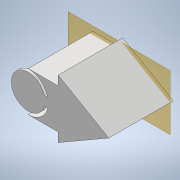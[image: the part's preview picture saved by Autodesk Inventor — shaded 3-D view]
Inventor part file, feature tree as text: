
AUTODESK INVENTOR PART (.ipt)
format: ipt  version: 2022.3 (Build 263350000, 350)  size: 201,216 bytes
history: native  units: mm
features: plane x5, reference x5, sketch x4, extrude x4, other x3
ambient origin geometry x8: Origin, YZ Plane, XZ Plane, XY Plane, X Axis, Y Axis, Z Axis, Center Point
bodies: Solid1 (feature_tree)
feature tree (21):
  sketch  "Sketch1"  dims[d0=10.0mm d1=0.0mm d2=0.2mm]
  other  "Work Point1"
  extrude  "Extrusion1"  Depth=10.0mm
  plane  "Work Plane1"
  sketch  "Sketch2"  dims[d3=1.0mm d4=10.0mm d5=0.0mm]
  plane  "Work Plane2"
  extrude  "Extrusion2"  Depth=10.0mm TaperAngle=0.0deg
  plane  "Work Plane3"
  sketch  "Sketch3"  dims[d6=10.0mm d7=0.0mm d8=2.0mm d9=0.0mm]
  plane  "Work Plane4"
  extrude  "Extrusion3"  Depth=2.0mm TaperAngle=0.0deg
  plane  "Work Plane5"
  extrude  "Extrusion4"  [1 undecoded]
  reference  "Reference1"
  reference  "Reference2"
  reference  "Reference3"
  sketch  "Sketch4"
  reference  "Reference4"
  reference  "Reference5"
  other  "Assembly2"
  other  "Base:1"
note: 1 required parameter value undecoded (feature->parameter linkage not recoverable at this tier; creation-order binding heuristic only, values carry confidence <= 0.55)
